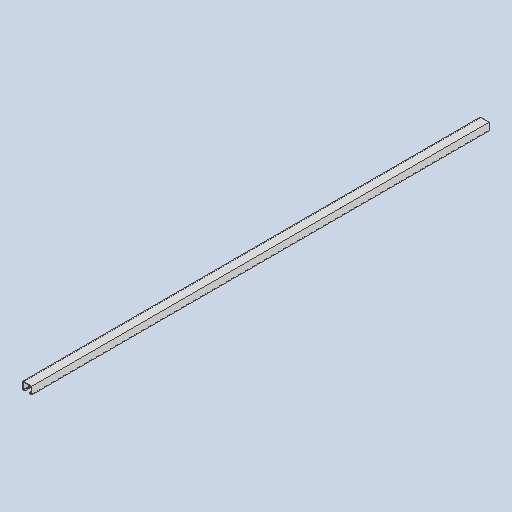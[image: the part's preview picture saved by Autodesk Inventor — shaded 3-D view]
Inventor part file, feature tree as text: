
AUTODESK INVENTOR PART (.ipt)
format: ipt  version: 2023 (Build 270158030, 158C)  size: 102,912 bytes
history: native  units: in
note: dims shown in document units (in); Inventor stores cm internally (conversion verified against a paired STEP export)
features: extrude x1, sketch x1
ambient origin geometry x8: Origin, YZ Plane, XZ Plane, XY Plane, X Axis, Y Axis, Z Axis, Center Point
bodies: Solid1 (feature_tree)
feature tree (2):
  extrude  "Extrusion1"  Depth=1.375in
  sketch  "Sketch1"  dims[d0=1.625in d1=1.375in d4=0.375in d5=0.2812in d6=0.1024in d7=0.1024in d8=0.1024in d9=0.1024in d11=0.1024in d12=0.1024in d13=0.2812in d14=0.1024in d15=84.0in d16=0.0in]
